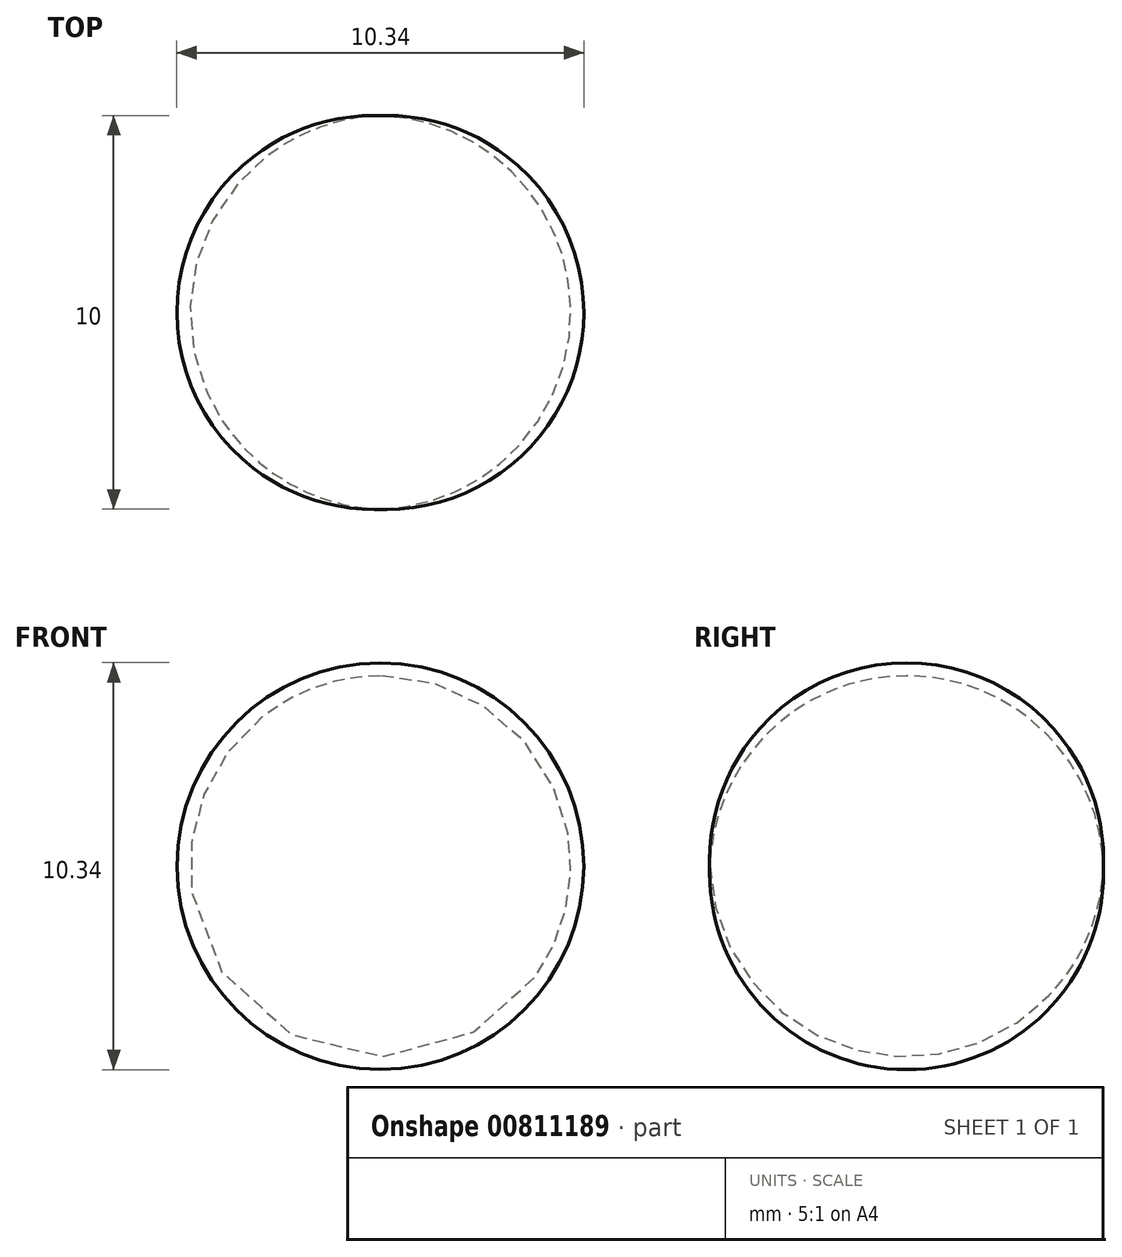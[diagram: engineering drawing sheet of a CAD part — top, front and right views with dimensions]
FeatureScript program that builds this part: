
annotation { "Feature Type Name" : "Feature", "Feature Type Description" : "" }
export const myFeature = defineFeature(function(context is Context, id is Id, definition is map)
    precondition{}
    {
        {
            var Q0;
            Q0=qCreatedBy(makeId("Top.planeOp"),FACE);
            var sketch = newSketch(context, id + "F0", { "sketchPlane" : qUnion([Q0])});
            skLineSegment(sketch, "E0", {"start": v(0, 0) * mm, "end": v(0, -5) * mm});
            skLineSegment(sketch, "E1", {"start": v(0, -5) * mm, "end": v(0, 5) * mm});
            skArc(sketch, "E2", {"start": v(0, -5) * mm, "mid": v(4.84, 0) * mm, "end": v(0, 5) * mm});
            skSolve(sketch);
        }
        {
            var Q0;
            {var subQ0=sQuery(id+"F0.wireOp",EDGE,"E2");Q0=makeQuery(id+"F0.imprint","IMPRINT",FACE,{"disambiguationData":[TD([[makeQuery(id+"F0.imprint","IMPRINT",EDGE,{"derivedFrom":subQ0}),1.0]])]});}
            var Q1;
            Q1=sQuery(id+"F0.wireOp",EDGE,"E1");
            revolve(context, id + "F1", {"surfaceOperationType" : NewSurfaceOperationType.NEW, "entities" : qUnion([Q0]), "axis" : qUnion([Q1]), "revolveType" : RevolveType.FULL});
        }
    });
